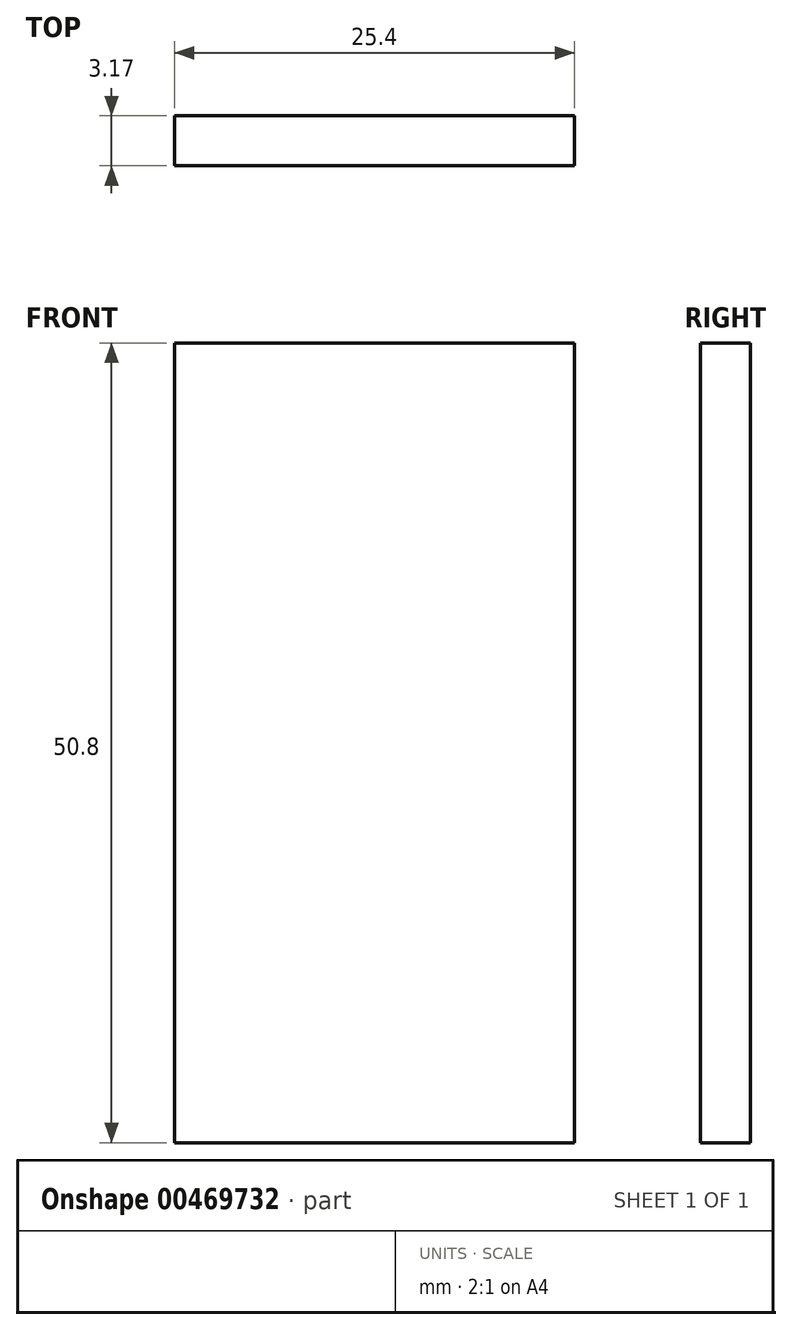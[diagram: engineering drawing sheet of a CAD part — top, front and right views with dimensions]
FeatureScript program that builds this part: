
annotation { "Feature Type Name" : "Feature", "Feature Type Description" : "" }
export const myFeature = defineFeature(function(context is Context, id is Id, definition is map)
    precondition{}
    {
        {
            var Q0;
            Q0=qCreatedBy(makeId("Right.planeOp"),FACE);
            var sketch = newSketch(context, id + "F0", { "sketchPlane" : qUnion([Q0])});
            skLineSegment(sketch, "E0.bottom", {"start": v(0, 0) * mm, "end": v(-3.18, 0) * mm});
            skLineSegment(sketch, "E0.top", {"start": v(0, -50.8) * mm, "end": v(-3.17, -50.8) * mm});
            skLineSegment(sketch, "E0.left", {"start": v(0, 0) * mm, "end": v(0, -50.8) * mm});
            skLineSegment(sketch, "E0.right", {"start": v(-3.18, 0) * mm, "end": v(-3.17, -50.8) * mm});
            skSolve(sketch);
        }
        {
            var Q0;
            Q0=makeQuery(id+"F0.imprint","IMPRINT",FACE,{"disambiguationData":[TD([[makeQuery(id+"F0.imprint","IMPRINT",EDGE,{"derivedFrom":sQuery(id+"F0.wireOp",EDGE,"E0.bottom")}),1.0]])]});
            extrude(context, id + "F1", {"entities" : qUnion([Q0]), "depth" : 25.4 * mm, "offsetDistance" : 25.4 * mm});
        }
    });
